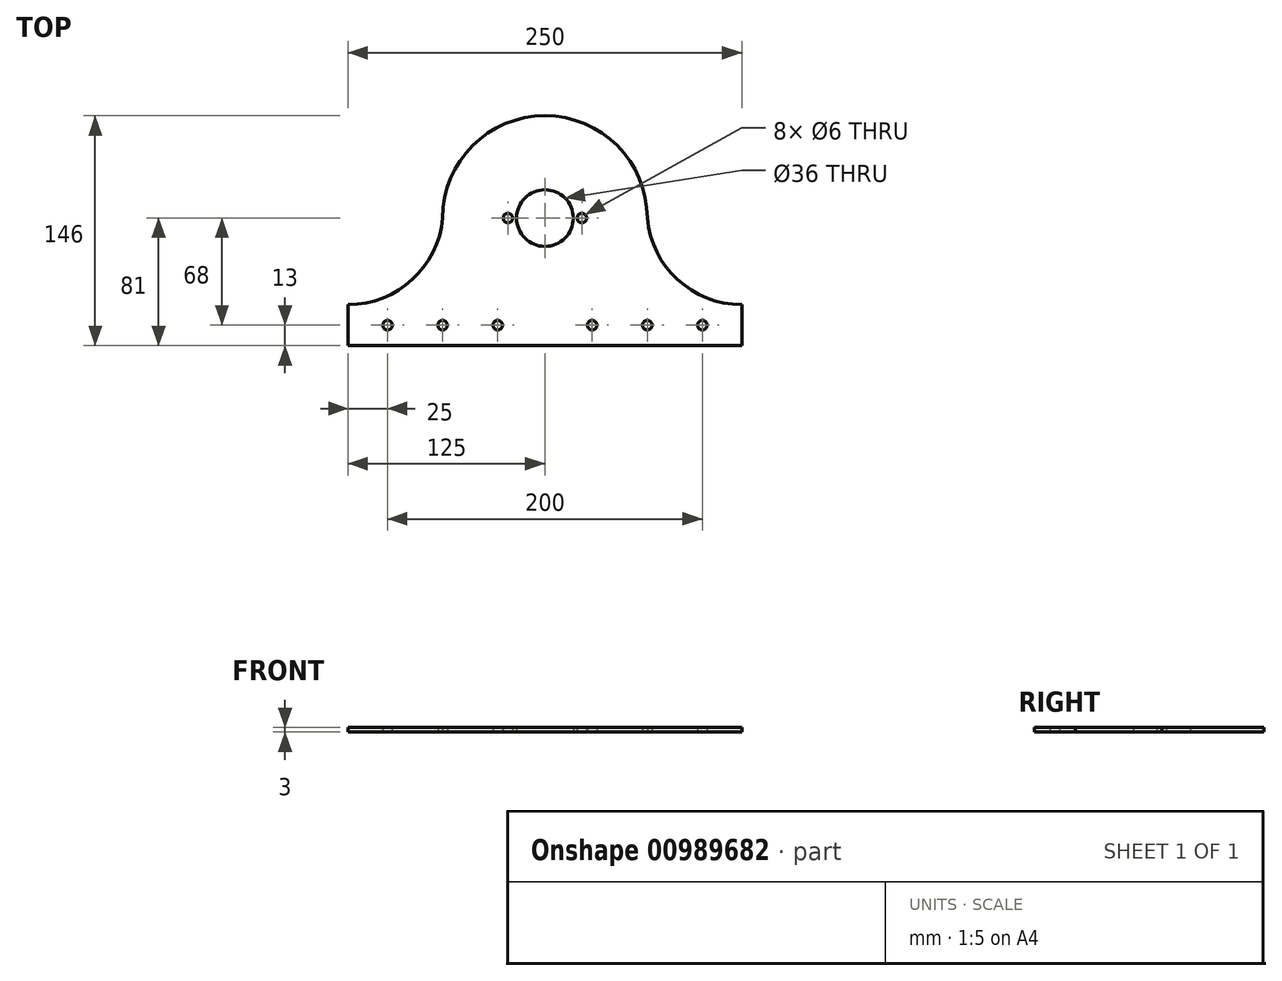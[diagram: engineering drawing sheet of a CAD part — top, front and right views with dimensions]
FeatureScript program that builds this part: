
annotation { "Feature Type Name" : "Feature", "Feature Type Description" : "" }
export const myFeature = defineFeature(function(context is Context, id is Id, definition is map)
    precondition{}
    {
        {
            var Q0;
            Q0=qCreatedBy(makeId("Top.planeOp"),FACE);
            var sketch = newSketch(context, id + "F0", { "sketchPlane" : qUnion([Q0])});
            skCircle(sketch, "E0", {"center": v(0, 0) * mm, "radius": 18 * mm});
            skCircle(sketch, "E1", {"center": v(23.5, 0) * mm, "radius": 3 * mm});
            skCircle(sketch, "E2", {"center": v(-23.5, 0) * mm, "radius": 3 * mm});
            skArc(sketch, "E3", {"start": v(65, 0) * mm, "mid": v(0, 65) * mm, "end": v(-65, 0) * mm});
            skLineSegment(sketch, "E4", {"start": v(-125, -81) * mm, "end": v(125, -81) * mm});
            skLineSegment(sketch, "E5", {"start": v(-125, -81) * mm, "end": v(-125, -55) * mm});
            skLineSegment(sketch, "E6", {"start": v(125, -81) * mm, "end": v(125, -55) * mm});
            skArc(sketch, "E7", {"start": v(65, 0) * mm, "mid": v(84.3, -39.17) * mm, "end": v(125, -55) * mm});
            skLineSegment(sketch, "E8", {"start": v(0, 0) * mm, "end": v(0, -42.45) * mm, "construction": true});
            skCircle(sketch, "E9", {"center": v(100, -68) * mm, "radius": 3 * mm});
            skPoint(sketch, "E9.centerSnap0", {"position": v(125, -68) * mm});
            skCircle(sketch, "E10", {"center": v(65, -68) * mm, "radius": 3 * mm});
            skCircle(sketch, "E11", {"center": v(30, -68) * mm, "radius": 3 * mm});
            skCircle(sketch, "E12.MirrorC", {"center": v(-30, -68) * mm, "radius": 3 * mm});
            skCircle(sketch, "E13.MirrorC", {"center": v(-65, -68) * mm, "radius": 3 * mm});
            skCircle(sketch, "E14.MirrorC", {"center": v(-100, -68) * mm, "radius": 3 * mm});
            skArc(sketch, "E15.MirrorCS", {"start": v(-65, 0) * mm, "mid": v(-84.3, -39.17) * mm, "end": v(-125, -55) * mm});
            skSolve(sketch);
        }
        {
            var Q0;
            Q0 = qSketchRegion(id + "F0", true);
            extrude(context, id + "F1", {"entities" : qUnion([Q0]), "depth" : 3 * mm, "offsetDistance" : 25 * mm});
        }
    });
